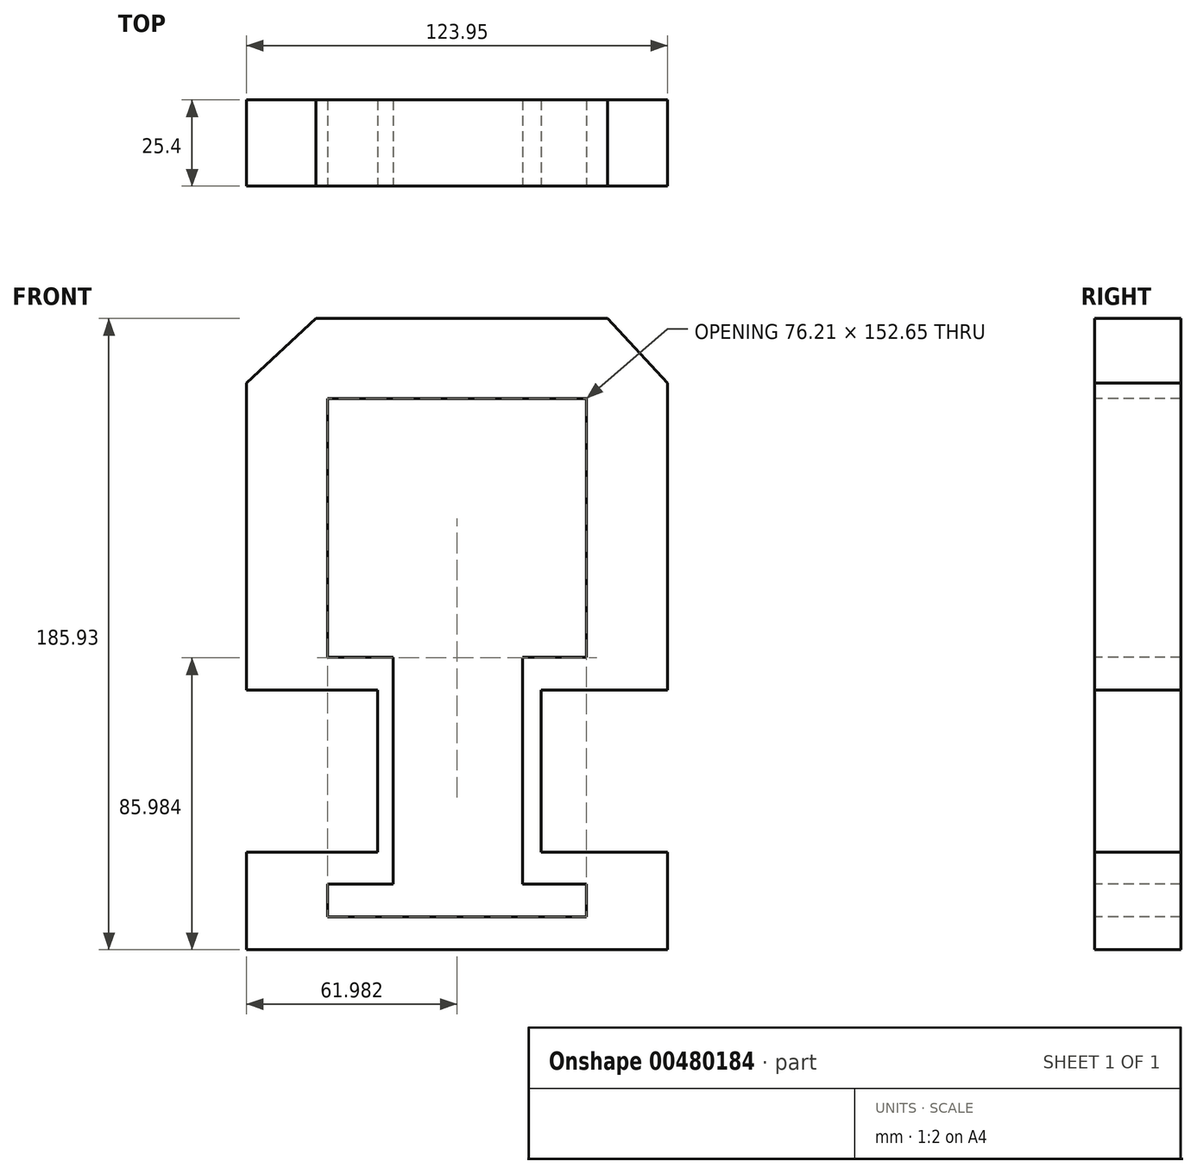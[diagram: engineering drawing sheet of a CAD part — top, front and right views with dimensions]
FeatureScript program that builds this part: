
annotation { "Feature Type Name" : "Feature", "Feature Type Description" : "" }
export const myFeature = defineFeature(function(context is Context, id is Id, definition is map)
    precondition{}
    {
        {
            var Q0;
            Q0=qCreatedBy(makeId("Front.planeOp"),FACE);
            var sketch = newSketch(context, id + "F0", { "sketchPlane" : qUnion([Q0])});
            skLineSegment(sketch, "E0", {"start": v(-58.6, -55.93) * mm, "end": v(65.34, -55.93) * mm});
            skLineSegment(sketch, "E1", {"start": v(65.34, -55.93) * mm, "end": v(65.34, 110.95) * mm});
            skLineSegment(sketch, "E2", {"start": v(-58.6, -55.93) * mm, "end": v(-58.6, 110.95) * mm});
            skLineSegment(sketch, "E3", {"start": v(-38.13, 130) * mm, "end": v(47.73, 130) * mm});
            skLineSegment(sketch, "E4", {"start": v(-58.6, 110.95) * mm, "end": v(-38.13, 130) * mm});
            skLineSegment(sketch, "E5", {"start": v(47.73, 130) * mm, "end": v(65.34, 110.95) * mm});
            skSolve(sketch);
        }
        {
            var Q0;
            Q0=makeQuery(id+"F0.imprint","IMPRINT",FACE,{"disambiguationData":[TD([[makeQuery(id+"F0.imprint","IMPRINT",EDGE,{"derivedFrom":sQuery(id+"F0.wireOp",EDGE,"E0")}),1.0]])]});
            extrude(context, id + "F1", {"entities" : qUnion([Q0]), "depth" : 25.4 * mm});
        }
        {
            var Q0;
            Q0=makeQuery(id+"F1.opExtrude","CAP_FACE",FACE,{"disambiguationData":[OSD([sQuery(id+"F0.wireOp",EDGE,"E0"),sQuery(id+"F0.wireOp",EDGE,"E1"),sQuery(id+"F0.wireOp",EDGE,"E2"),sQuery(id+"F0.wireOp",EDGE,"E3"),sQuery(id+"F0.wireOp",EDGE,"E4"),sQuery(id+"F0.wireOp",EDGE,"E5")])],"isStart":false});
            var sketch = newSketch(context, id + "F2", { "sketchPlane" : qUnion([Q0])});
            skLineSegment(sketch, "E6.bottom", {"start": v(-34.73, -36.62) * mm, "end": v(41.47, -36.62) * mm});
            skLineSegment(sketch, "E6.top", {"start": v(-34.73, -46.27) * mm, "end": v(41.47, -46.27) * mm});
            skLineSegment(sketch, "E6.left", {"start": v(-34.73, -36.62) * mm, "end": v(-34.73, -46.27) * mm});
            skLineSegment(sketch, "E6.right", {"start": v(41.47, -36.62) * mm, "end": v(41.47, -46.27) * mm});
            skSolve(sketch);
        }
        {
            var Q0;
            Q0=makeQuery(id+"F2.imprint","IMPRINT",FACE,{"disambiguationData":[TD([[makeQuery(id+"F2.imprint","IMPRINT",EDGE,{"derivedFrom":sQuery(id+"F2.wireOp",EDGE,"E6.bottom")}),-1.0]])]});
            extrude(context, id + "F3", {"entities" : qUnion([Q0]), "operationType" : NewBodyOperationType.REMOVE, "oppositeDirection" : true, "depth" : 25.4 * mm});
        }
        {
            var Q0;
            Q0=makeQuery(id+"F1.opExtrude","CAP_FACE",FACE,{"disambiguationData":[OSD([sQuery(id+"F0.wireOp",EDGE,"E0"),sQuery(id+"F0.wireOp",EDGE,"E1"),sQuery(id+"F0.wireOp",EDGE,"E2"),sQuery(id+"F0.wireOp",EDGE,"E3"),sQuery(id+"F0.wireOp",EDGE,"E4"),sQuery(id+"F0.wireOp",EDGE,"E5")])],"isStart":false});
            var sketch = newSketch(context, id + "F4", { "sketchPlane" : qUnion([Q0])});
            skLineSegment(sketch, "E7.bottom", {"start": v(-58.6, -27.22) * mm, "end": v(-20, -27.22) * mm});
            skLineSegment(sketch, "E7.top", {"start": v(-58.6, 20.53) * mm, "end": v(-20, 20.53) * mm});
            skLineSegment(sketch, "E7.left", {"start": v(-58.6, -27.22) * mm, "end": v(-58.6, 20.53) * mm});
            skLineSegment(sketch, "E7.right", {"start": v(-20, -27.22) * mm, "end": v(-20, 20.53) * mm});
            skLineSegment(sketch, "E8.bottom", {"start": v(65.34, -27.22) * mm, "end": v(28.17, -27.22) * mm});
            skLineSegment(sketch, "E8.top", {"start": v(65.34, 20.53) * mm, "end": v(28.17, 20.53) * mm});
            skLineSegment(sketch, "E8.left", {"start": v(65.34, -27.22) * mm, "end": v(65.34, 20.53) * mm});
            skLineSegment(sketch, "E8.right", {"start": v(28.17, -27.22) * mm, "end": v(28.17, 20.53) * mm});
            skSolve(sketch);
        }
        {
            var Q0;
            {var subQ4=sQuery(id+"F4.wireOp",EDGE,"E7.bottom");Q0=makeQuery(id+"F4.imprint","IMPRINT",FACE,{"disambiguationData":[TD([[makeQuery(id+"F4.imprint","IMPRINT",EDGE,{"derivedFrom":subQ4}),-1.0]])]});}
            var sketch = newSketch(context, id + "F5", { "sketchPlane" : qUnion([Q0])});
            skLineSegment(sketch, "E9.bottom", {"start": v(-15.46, -36.62) * mm, "end": v(22.64, -36.62) * mm});
            skLineSegment(sketch, "E9.top", {"start": v(-15.46, 30.18) * mm, "end": v(22.64, 30.18) * mm});
            skLineSegment(sketch, "E9.left", {"start": v(-15.46, -36.62) * mm, "end": v(-15.46, 30.18) * mm});
            skLineSegment(sketch, "E9.right", {"start": v(22.64, -36.62) * mm, "end": v(22.64, 30.18) * mm});
            skSolve(sketch);
        }
        {
            var Q0;
            Q0 = qSketchRegion(id + "F5", true);
            extrude(context, id + "F6", {"entities" : qUnion([Q0]), "operationType" : NewBodyOperationType.REMOVE, "oppositeDirection" : true, "depth" : 25.4 * mm});
        }
        {
            var Q0;
            Q0 = qSketchRegion(id + "F4", true);
            extrude(context, id + "F7", {"entities" : qUnion([Q0]), "operationType" : NewBodyOperationType.REMOVE, "oppositeDirection" : true, "depth" : 25.4 * mm});
        }
        {
            var Q0;
            Q0=makeQuery(id+"F1.opExtrude","CAP_FACE",FACE,{"disambiguationData":[OSD([sQuery(id+"F0.wireOp",EDGE,"E0"),sQuery(id+"F0.wireOp",EDGE,"E1"),sQuery(id+"F0.wireOp",EDGE,"E2"),sQuery(id+"F0.wireOp",EDGE,"E3"),sQuery(id+"F0.wireOp",EDGE,"E4"),sQuery(id+"F0.wireOp",EDGE,"E5")])],"isStart":false});
            var sketch = newSketch(context, id + "F8", { "sketchPlane" : qUnion([Q0])});
            skLineSegment(sketch, "E10.bottom", {"start": v(-34.72, 30.18) * mm, "end": v(41.48, 30.18) * mm});
            skLineSegment(sketch, "E10.top", {"start": v(-34.72, 106.38) * mm, "end": v(41.48, 106.38) * mm});
            skLineSegment(sketch, "E10.left", {"start": v(-34.72, 30.18) * mm, "end": v(-34.72, 106.38) * mm});
            skLineSegment(sketch, "E10.right", {"start": v(41.48, 30.18) * mm, "end": v(41.48, 106.38) * mm});
            skSolve(sketch);
        }
        {
            var Q0;
            Q0 = qSketchRegion(id + "F8", true);
            extrude(context, id + "F9", {"entities" : qUnion([Q0]), "operationType" : NewBodyOperationType.REMOVE, "oppositeDirection" : true, "depth" : 25.4 * mm});
        }
    });
